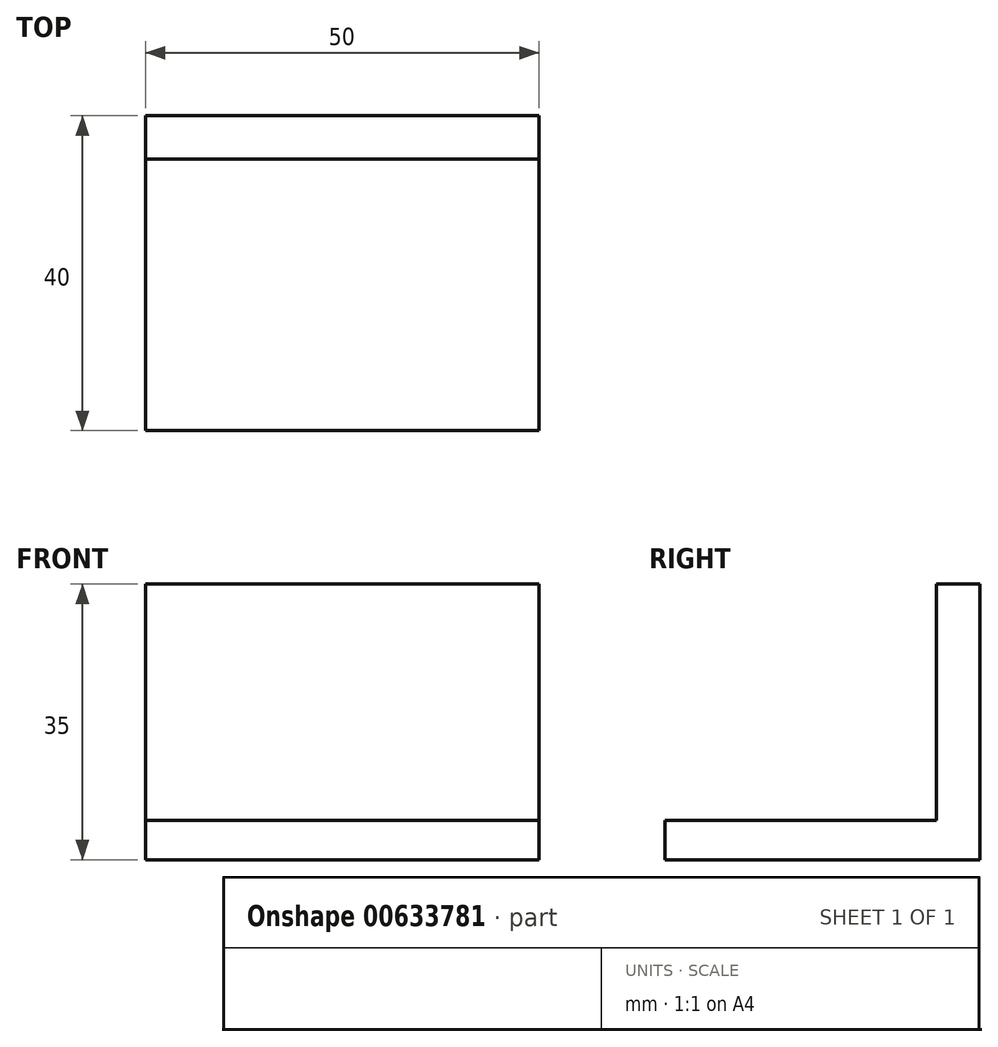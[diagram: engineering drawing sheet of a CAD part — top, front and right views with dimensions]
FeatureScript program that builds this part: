
annotation { "Feature Type Name" : "Feature", "Feature Type Description" : "" }
export const myFeature = defineFeature(function(context is Context, id is Id, definition is map)
    precondition{}
    {
        {
            var Q0;
            Q0=qCreatedBy(makeId("Front.planeOp"),FACE);
            var sketch = newSketch(context, id + "F0", { "sketchPlane" : qUnion([Q0])});
            skLineSegment(sketch, "E0.bottom", {"start": v(25, 2.5) * mm, "end": v(-25, 2.5) * mm});
            skLineSegment(sketch, "E0.top", {"start": v(25, -2.5) * mm, "end": v(-25, -2.5) * mm});
            skLineSegment(sketch, "E0.left", {"start": v(25, 2.5) * mm, "end": v(25, -2.5) * mm});
            skLineSegment(sketch, "E0.right", {"start": v(-25, 2.5) * mm, "end": v(-25, -2.5) * mm});
            skPoint(sketch, "E0.middle", {"position": v(0, 0) * mm});
            skSolve(sketch);
        }
        {
            var Q0;
            Q0 = qSketchRegion(id + "F0", true);
            extrude(context, id + "F1", {"entities" : qUnion([Q0]), "depth" : 40 * mm, "offsetDistance" : 25 * mm});
        }
        {
            var Q0;
            Q0=makeQuery(id+"F1.opExtrude","SWEPT_FACE",FACE,{"disambiguationData":[OSD([sQuery(id+"F0.wireOp",EDGE,"E0.bottom")])]});
            var sketch = newSketch(context, id + "F2", { "sketchPlane" : qUnion([Q0])});
            skLineSegment(sketch, "E1.bottom", {"start": v(25, 0) * mm, "end": v(-25, 0) * mm});
            skLineSegment(sketch, "E1.top", {"start": v(25, -5.5) * mm, "end": v(-25, -5.5) * mm});
            skLineSegment(sketch, "E1.left", {"start": v(25, 0) * mm, "end": v(25, -5.5) * mm});
            skLineSegment(sketch, "E1.right", {"start": v(-25, 0) * mm, "end": v(-25, -5.5) * mm});
            skPoint(sketch, "E1.middle", {"position": v(0, -2.75) * mm});
            skSolve(sketch);
        }
        {
            var Q0;
            Q0=makeQuery(id+"F2.imprint","IMPRINT",FACE,{"disambiguationData":[TD([[makeQuery(id+"F2.imprint","IMPRINT",EDGE,{"derivedFrom":sQuery(id+"F2.wireOp",EDGE,"E1.bottom")}),1.0]])]});
            extrude(context, id + "F3", {"entities" : qUnion([Q0]), "operationType" : NewBodyOperationType.ADD, "depth" : 30 * mm, "offsetDistance" : 25 * mm});
        }
    });
